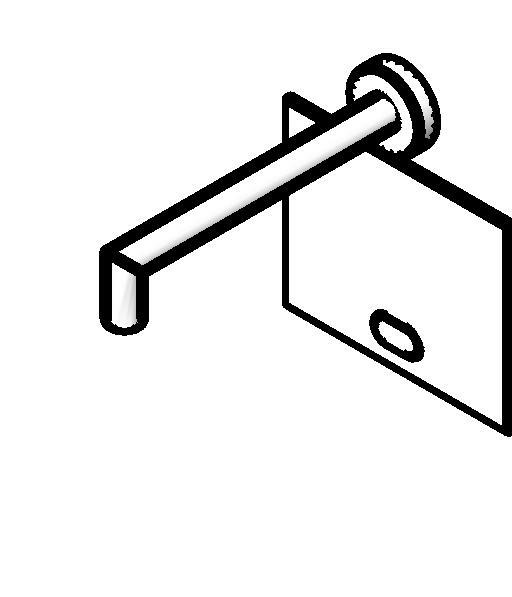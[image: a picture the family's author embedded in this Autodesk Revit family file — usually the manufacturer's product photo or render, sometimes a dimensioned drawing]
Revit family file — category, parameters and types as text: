
# Revit family: Deca_Torneira embutida de parede com sensor bivolt para lavatório_Decalux_1780
name_source: partatom
category: Plumbing Fixtures
units: mm (PartAtom-declared; Revit-internal decimal feet)

## family parameters
Cut with Voids When Loaded = No
Host = Face
Part Type = Normal
Room Calculation Point = No
Round Connector Dimension = Use Radius
Shared = No

## types (1)
- 1780.C_Cromado
    Acompanha o Produto = Acompanha restritor de vazão 6L/Min
    Aprovado por = quattroD
    Atendimento ao Cliente = 0800-0117073
    CWFU = 0
    Categoria = USO PUBLICO
    Composição Anel Vedação = -
    Composição Assento = -
    Composição Básica = Liga de Cobre (bronze e latão),Plásticos de Engenharia,Elastômeros,Eletrônicos
    Composição Componente = -
    Consumo = -
    Cor Interna = -
    Cor Principal = Cromado
    Cor Secundária = -
    Cores Componente = -
    Criado por = quattroD
    Código Pai = 1780
    Default Elevation = 1200 mm
    Description = Torneira embutida de parede com sensor bivolt para lavatório
    Diâmetro Água Fria = 15 mm  [stored 0.0492126 ft]
    HWFU = 0
    Informações Complementares = -
    Itens de Instalação = -
    Linha = Decalux
    Manufacturer = Deca
    Material = Deca_Cromado
    Model = 1780.C
    Norma = Não Possui
    Peso Líquido (Kg) = 1.828
    Pressão máx. funcionamento = 40 MCA
    Pressão mín. Aquec. Acúmulo = -
    Pressão mín. Aquec. Passagem = -
    Pressão mín. funcionamento = 2 MCA
    Raio Água Fria = 8 mm  [stored 0.0262467 ft]
    Saída de Esgoto = -
    Segmento = Banheiro Médio
    Tipo de dispositivo economizador = Sim
    Tipo de mecanismo utilizado = Solenóide
    Tipo de rosca de entrada = BSP NBR 8133
    Tipo de rosca de saída = -
    URL = www.deca.com.br
    Vazão na Pressão máx. (L/min) = 6
    Vazão na Pressão mín. (L/min) = 4

note: source unit labels omitted for Vazão na Pressão máx. (L/min), Vazão na Pressão mín. (L/min) — the stored unit's dimension contradicts the parameter name (converter mislabeling)

note: [stored X ft] marks values corroborated as IEEE doubles in the binary element streams (Revit-internal decimal feet)

## geometry (parser evidence)
native form markers: Sweep x3
no freeform markers — native parametric forms only
